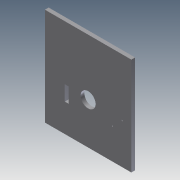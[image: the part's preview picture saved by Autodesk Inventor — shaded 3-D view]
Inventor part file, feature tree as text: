
AUTODESK INVENTOR PART (.ipt)
format: ipt  version: 2011 (Build 150239000, 239)  size: 290,304 bytes
history: native  units: in
note: dims shown in document units (in); Inventor stores cm internally (conversion verified against a paired STEP export)
features: extrude x27, sketch x27
ambient origin geometry x8: Origin, YZ Plane, XZ Plane, XY Plane, X Axis, Y Axis, Z Axis, Center Point
bodies: Solid1 (feature_tree)
feature tree (54):
  extrude  "Extrusion1"  Depth=5.0in
  extrude  "Extrusion2"  Depth=2.0in
  extrude  "Extrusion3"  Depth=0.25in
  extrude  "Extrusion4"  Depth=1.2598in
  extrude  "Extrusion5"  Depth=0.5in TaperAngle=0.0deg
  extrude  "Extrusion6"  Depth=0.9055in
  extrude  "Extrusion7"  Depth=0.25in
  extrude  "Extrusion8"  Depth=0.5in TaperAngle=0.0deg
  extrude  "Extrusion9"  Depth=0.25in TaperAngle=0.0deg
  extrude  "Extrusion10"  Depth=0.25in TaperAngle=0.0deg
  extrude  "Extrusion11"  Depth=0.25in TaperAngle=0.0deg
  extrude  "Extrusion12"  Depth=0.315in
  extrude  "Extrusion13"  Depth=0.6299in
  extrude  "Extrusion14"  Depth=0.0787in
  extrude  "Extrusion15"  Depth=0.3in TaperAngle=0.0deg
  extrude  "Extrusion16"  Depth=0.1299in
  extrude  "Extrusion17"  Depth=0.1299in
  extrude  "Extrusion18"  Depth=0.05in TaperAngle=0.0deg
  extrude  "Extrusion19"  Depth=0.25in
  extrude  "Extrusion20"  Depth=7.0in TaperAngle=0.0deg
  extrude  "Extrusion21"  Depth=1.0in
  extrude  "Extrusion22"  Depth=2.75in
  extrude  "Extrusion23"  Depth=1.0in TaperAngle=0.0deg
  extrude  "Extrusion24"  Depth=0.5in TaperAngle=0.0deg
  extrude  "Extrusion25"  Depth=0.125in TaperAngle=0.0deg
  extrude  "Extrusion26"  Depth=0.25in TaperAngle=0.0deg
  extrude  "Extrusion27"  Depth=0.25in TaperAngle=0.0deg
  sketch  "Sketch1"  dims[d0=5.0in d1=5.0in]
  sketch  "Sketch2"  dims[d2=0.25in d3=0.0in d4=2.0in]
  sketch  "Sketch3"  dims[d5=0.9055in d6=0.25in]
  sketch  "Sketch4"  dims[d7=1.5748in d8=1.2598in]
  sketch  "Sketch5"  dims[d9=0.25in d10=0.0in d11=0.5in d12=0.0in]
  sketch  "Sketch6"  dims[d13=0.5in d14=0.0in d15=0.9055in]
  sketch  "Sketch7"  dims[d16=0.25in d17=0.25in]
  sketch  "Sketch8"  dims[d18=1.0in d19=0.5in d20=0.0in]
  sketch  "Sketch9"  dims[d21=0.5in d22=0.0in d23=0.25in d24=0.0in]
  sketch  "Sketch10"  dims[d25=4.2795in d26=0.25in d27=0.0in]
  sketch  "Sketch11"  dims[d28=0.25in d29=0.25in d30=0.0in]
  sketch  "Sketch12"  dims[d31=0.4724in d32=0.315in]
  sketch  "Sketch13"  dims[d33=0.6299in d34=0.6299in]
  sketch  "Sketch14"  dims[d35=0.0787in d36=0.0787in]
  sketch  "Sketch15"  dims[d37=0.25in d38=0.0in d39=0.3in d40=0.0in]
  sketch  "Sketch16"  dims[d41=0.3in d42=0.0in d43=0.1299in]
  sketch  "Sketch17"  dims[d44=0.3in d45=0.0in d46=0.1299in]
  sketch  "Sketch18"  dims[d47=0.3in d48=0.0in d49=0.05in d50=0.0in]
  sketch  "Sketch19"  dims[d51=1.0in d52=0.0in d53=0.25in]
  sketch  "Sketch20"  dims[d54=0.25in d55=7.0in d56=0.0in]
  sketch  "Sketch21"  dims[d57=1.0in d58=1.0in]
  sketch  "Sketch22"  dims[d59=1.0in d60=0.0in d61=2.75in]
  sketch  "Sketch23"  dims[d62=1.0in d63=1.0in d64=0.0in]
  sketch  "Sketch24"  dims[d65=0.25in d66=0.0in d67=0.5in d68=0.0in]
  sketch  "Sketch25"  dims[d69=0.125in d70=0.0in d71=0.125in d72=0.0in]
  sketch  "Sketch26"  dims[d73=0.125in d74=0.25in d75=0.0in]
  sketch  "Sketch27"  dims[d76=0.125in d77=0.25in d78=0.0in d79=0.125in d80=0.125in d81=0.25in d82=0.0in d83=0.25in d84=0.0in]
